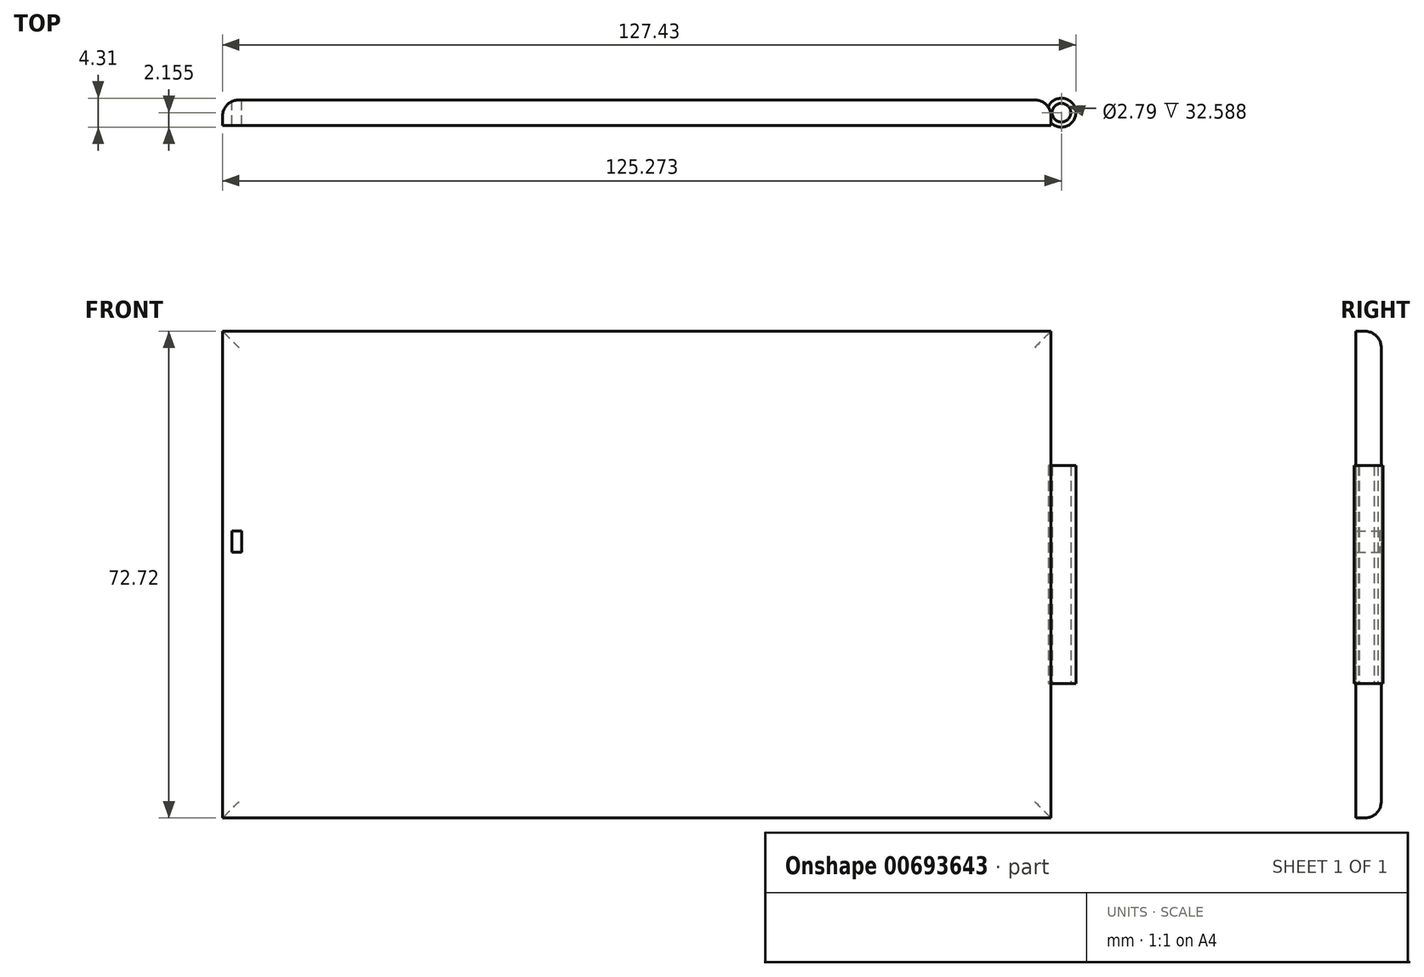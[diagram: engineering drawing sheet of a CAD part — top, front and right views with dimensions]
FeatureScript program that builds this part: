
annotation { "Feature Type Name" : "Feature", "Feature Type Description" : "" }
export const myFeature = defineFeature(function(context is Context, id is Id, definition is map)
    precondition{}
    {
        {
            var Q0;
            Q0=qCreatedBy(makeId("Front.planeOp"),FACE);
            var sketch = newSketch(context, id + "F0", { "sketchPlane" : qUnion([Q0])});
            skLineSegment(sketch, "E0.bottom", {"start": v(40.34, 48.46) * mm, "end": v(-83.38, 48.46) * mm});
            skLineSegment(sketch, "E0.top", {"start": v(40.34, -24.26) * mm, "end": v(-83.38, -24.26) * mm});
            skLineSegment(sketch, "E0.left", {"start": v(40.34, 48.46) * mm, "end": v(40.34, -24.26) * mm});
            skLineSegment(sketch, "E0.right", {"start": v(-83.38, 48.46) * mm, "end": v(-83.38, -24.26) * mm});
            skSolve(sketch);
        }
        {
            var Q0;
            Q0 = qSketchRegion(id + "F0", true);
            extrude(context, id + "F1", {"entities" : qUnion([Q0]), "depth" : 3.8 * mm, "offsetDistance" : 25.4 * mm});
        }
        {
            var Q0;
            Q0=makeQuery(id+"F1.opExtrude","SWEPT_FACE",FACE,{"disambiguationData":[OSD([sQuery(id+"F0.wireOp",EDGE,"E0.top")])]});
            var sketch = newSketch(context, id + "F2", { "sketchPlane" : qUnion([Q0])});
            skCircle(sketch, "E1", {"center": v(41.9, 1.9) * mm, "radius": 1.4 * mm});
            skPoint(sketch, "E1.centerSnap0", {"position": v(40.34, 1.9) * mm});
            skCircle(sketch, "E2", {"center": v(41.9, 1.9) * mm, "radius": 2.16 * mm});
            skSolve(sketch);
        }
        {
            var Q0;
            Q0 = qSketchRegion(id + "F2", true);
            extrude(context, id + "F3", {"entities" : qUnion([Q0]), "operationType" : NewBodyOperationType.ADD, "oppositeDirection" : true, "depth" : 72.72 * mm, "offsetDistance" : 25.4 * mm});
        }
        {
            var Q0;
            Q0=makeQuery(id+"F3.boolean.opBoolean","MERGE",FACE,{"derivedFrom":[makeQuery(id+"F1.opExtrude","SWEPT_FACE",FACE,{"disambiguationData":[OSD([sQuery(id+"F0.wireOp",EDGE,"E0.top")])]}),makeQuery(id+"F3.opExtrude","CAP_FACE",FACE,{"disambiguationData":[OSD([sQuery(id+"F2.wireOp",EDGE,"E1"),sQuery(id+"F2.wireOp",EDGE,"E2")])],"isStart":true})]});
            var sketch = newSketch(context, id + "F4", { "sketchPlane" : qUnion([Q0])});
            skLineSegment(sketch, "E3", {"start": v(40.34, 3.4) * mm, "end": v(40.34, 0.4) * mm});
            skSolve(sketch);
        }
        {
            var Q0;
            Q0=makeQuery(id+"F4.imprint","IMPRINT",FACE,{"disambiguationData":[TD([[makeQuery(id+"F4.imprint","IMPRINT",EDGE,{"derivedFrom":sQuery(id+"F4.wireOp",EDGE,"E3")}),1.0]])]});
            extrude(context, id + "F5", {"entities" : qUnion([Q0]), "operationType" : NewBodyOperationType.REMOVE, "oppositeDirection" : true, "depth" : 20.07 * mm, "offsetDistance" : 25.4 * mm});
        }
        {
            var Q0;
            Q0=makeQuery(id+"F3.boolean.opBoolean","MERGE",FACE,{"derivedFrom":[makeQuery(id+"F1.opExtrude","SWEPT_FACE",FACE,{"disambiguationData":[OSD([sQuery(id+"F0.wireOp",EDGE,"E0.bottom")])]}),makeQuery(id+"F3.opExtrude","CAP_FACE",FACE,{"disambiguationData":[OSD([sQuery(id+"F2.wireOp",EDGE,"E1"),sQuery(id+"F2.wireOp",EDGE,"E2")])],"isStart":false})]});
            var sketch = newSketch(context, id + "F6", { "sketchPlane" : qUnion([Q0])});
            skLineSegment(sketch, "E4", {"start": v(40.34, -0.4) * mm, "end": v(40.34, -3.4) * mm});
            skSolve(sketch);
        }
        {
            var Q0;
            Q0=makeQuery(id+"F6.imprint","IMPRINT",FACE,{"disambiguationData":[TD([[makeQuery(id+"F6.imprint","IMPRINT",EDGE,{"derivedFrom":sQuery(id+"F6.wireOp",EDGE,"E4")}),1.0]])]});
            extrude(context, id + "F7", {"entities" : qUnion([Q0]), "operationType" : NewBodyOperationType.REMOVE, "oppositeDirection" : true, "depth" : 20.07 * mm, "offsetDistance" : 25.4 * mm});
        }
        {
            var Q0;
            Q0=makeQuery(id+"F1.opExtrude","CAP_FACE",FACE,{"disambiguationData":[OSD([sQuery(id+"F0.wireOp",EDGE,"E0.bottom"),sQuery(id+"F0.wireOp",EDGE,"E0.top"),sQuery(id+"F0.wireOp",EDGE,"E0.left"),sQuery(id+"F0.wireOp",EDGE,"E0.right")])],"isStart":true});
            var sketch = newSketch(context, id + "F8", { "sketchPlane" : qUnion([Q0])});
            skLineSegment(sketch, "E5", {"start": v(80.52, 18.6) * mm, "end": v(80.52, 15.47) * mm});
            skLineSegment(sketch, "E6", {"start": v(80.52, 15.47) * mm, "end": v(81.96, 15.47) * mm});
            skLineSegment(sketch, "E7", {"start": v(81.96, 15.47) * mm, "end": v(81.96, 18.6) * mm});
            skLineSegment(sketch, "E8", {"start": v(81.96, 18.6) * mm, "end": v(80.52, 18.6) * mm});
            skSolve(sketch);
        }
        {
            var Q0;
            Q0 = qSketchRegion(id + "F8", true);
            extrude(context, id + "F9", {"entities" : qUnion([Q0]), "operationType" : NewBodyOperationType.REMOVE, "oppositeDirection" : true, "depth" : 25.4 * mm, "offsetDistance" : 25.4 * mm});
        }
        {
            var Q0;
            Q0=makeQuery(id+"F1.opExtrude","CAP_EDGE",EDGE,{"disambiguationData":[OSD([sQuery(id+"F0.wireOp",EDGE,"E0.bottom")])],"isStart":true});
            var Q1;
            Q1=makeQuery(id+"F1.opExtrude","CAP_EDGE",EDGE,{"disambiguationData":[OSD([sQuery(id+"F0.wireOp",EDGE,"E0.left")])],"isStart":true});
            var Q2;
            Q2=makeQuery(id+"F1.opExtrude","CAP_EDGE",EDGE,{"disambiguationData":[OSD([sQuery(id+"F0.wireOp",EDGE,"E0.top")])],"isStart":true});
            var Q3;
            Q3=makeQuery(id+"F1.opExtrude","CAP_EDGE",EDGE,{"disambiguationData":[OSD([sQuery(id+"F0.wireOp",EDGE,"E0.right")])],"isStart":true});
            fillet(context, id + "F10", {"entities" : qUnion([Q0, Q1, Q2, Q3]), "radius" : 2.45 * mm, "tangentPropagation" : true, "allowEdgeOverflow" : false});
        }
    });
